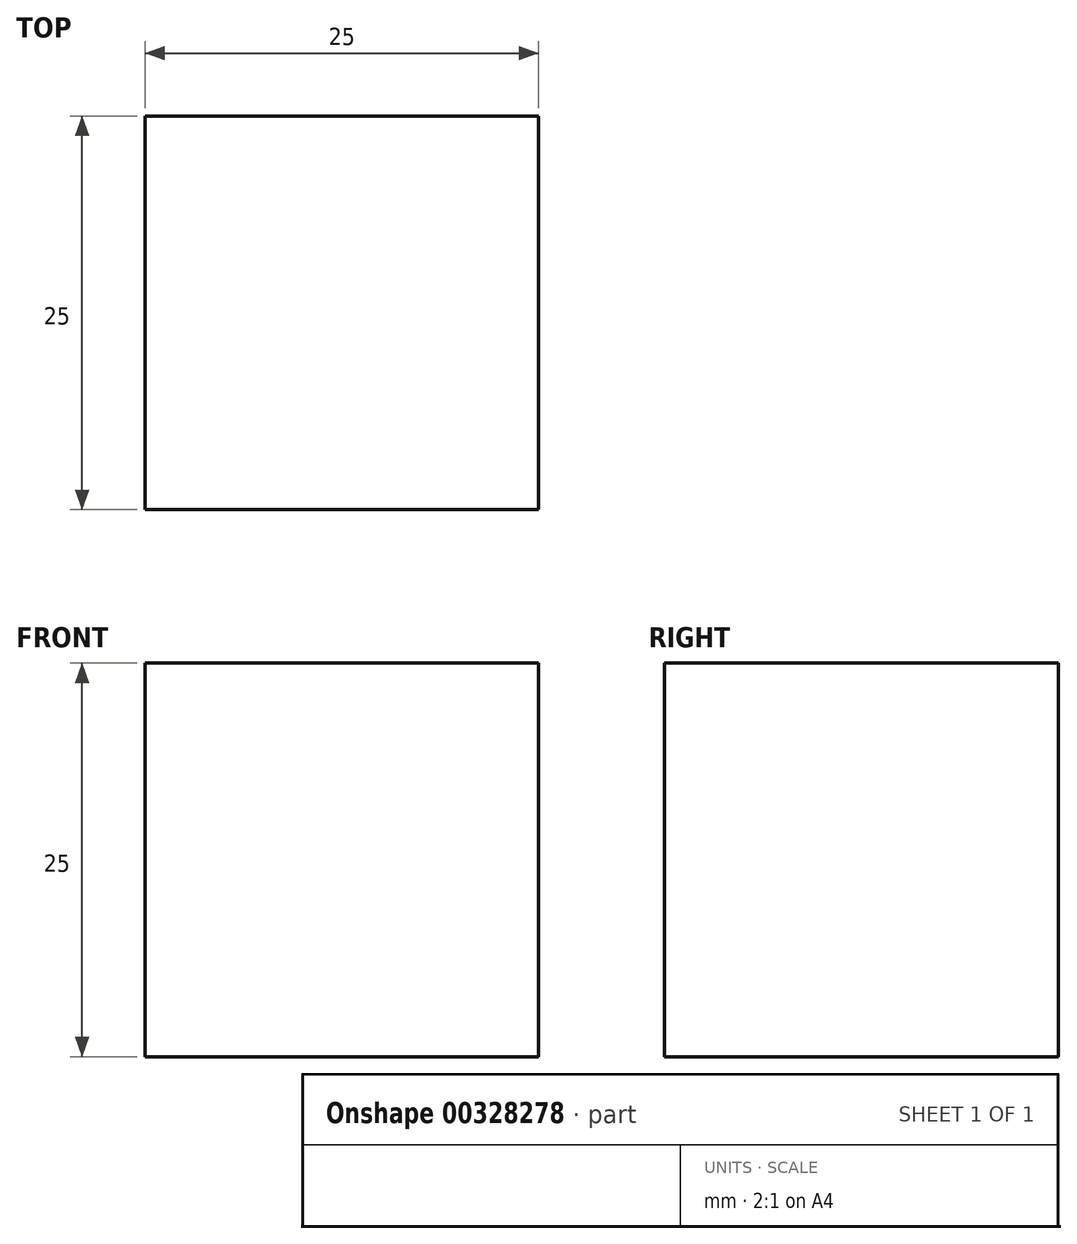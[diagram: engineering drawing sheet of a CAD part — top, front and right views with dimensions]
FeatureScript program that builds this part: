
annotation { "Feature Type Name" : "Feature", "Feature Type Description" : "" }
export const myFeature = defineFeature(function(context is Context, id is Id, definition is map)
    precondition{}
    {
        {
            var Q0;
            Q0=qCreatedBy(makeId("Top.planeOp"),FACE);
            var sketch = newSketch(context, id + "F0", { "sketchPlane" : qUnion([Q0])});
            skLineSegment(sketch, "E0.bottom", {"start": v(12.5, 12.5) * mm, "end": v(-12.5, 12.5) * mm});
            skLineSegment(sketch, "E0.top", {"start": v(12.5, -12.5) * mm, "end": v(-12.5, -12.5) * mm});
            skLineSegment(sketch, "E0.left", {"start": v(12.5, 12.5) * mm, "end": v(12.5, -12.5) * mm});
            skLineSegment(sketch, "E0.right", {"start": v(-12.5, 12.5) * mm, "end": v(-12.5, -12.5) * mm});
            skPoint(sketch, "E0.middle", {"position": v(0, 0) * mm});
            skSolve(sketch);
        }
        {
            var Q0;
            Q0 = qSketchRegion(id + "F0", true);
            extrude(context, id + "F1", {"entities" : qUnion([Q0]), "depth" : 25 * mm});
        }
    });
